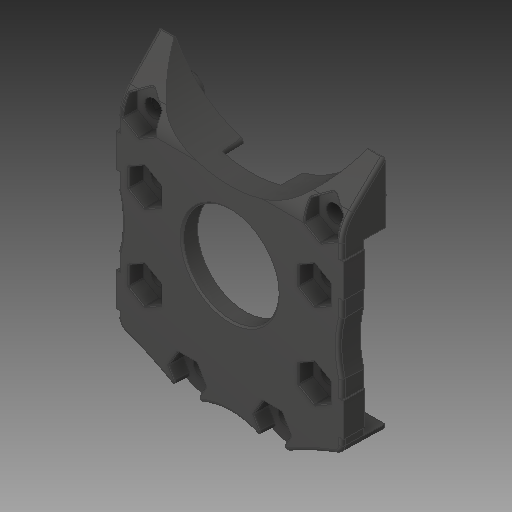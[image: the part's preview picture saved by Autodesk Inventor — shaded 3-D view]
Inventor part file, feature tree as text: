
AUTODESK INVENTOR PART (.ipt)
format: ipt  version: 2017 (Build 210142000, 142)  size: 3,076,096 bytes
history: native  units: in
note: dims shown in document units (in); Inventor stores cm internally (conversion verified against a paired STEP export)
features: chamfer x1
ambient origin geometry x8: Origin, YZ Plane, XZ Plane, XY Plane, X Axis, Y Axis, Z Axis, Center Point
bodies: Solid1 (feature_tree)
feature tree (1):
  chamfer  "Chamfer3"  [1 undecoded]
note: 1 required parameter value undecoded (feature->parameter linkage not recoverable at this tier; creation-order binding heuristic only, values carry confidence <= 0.55)
